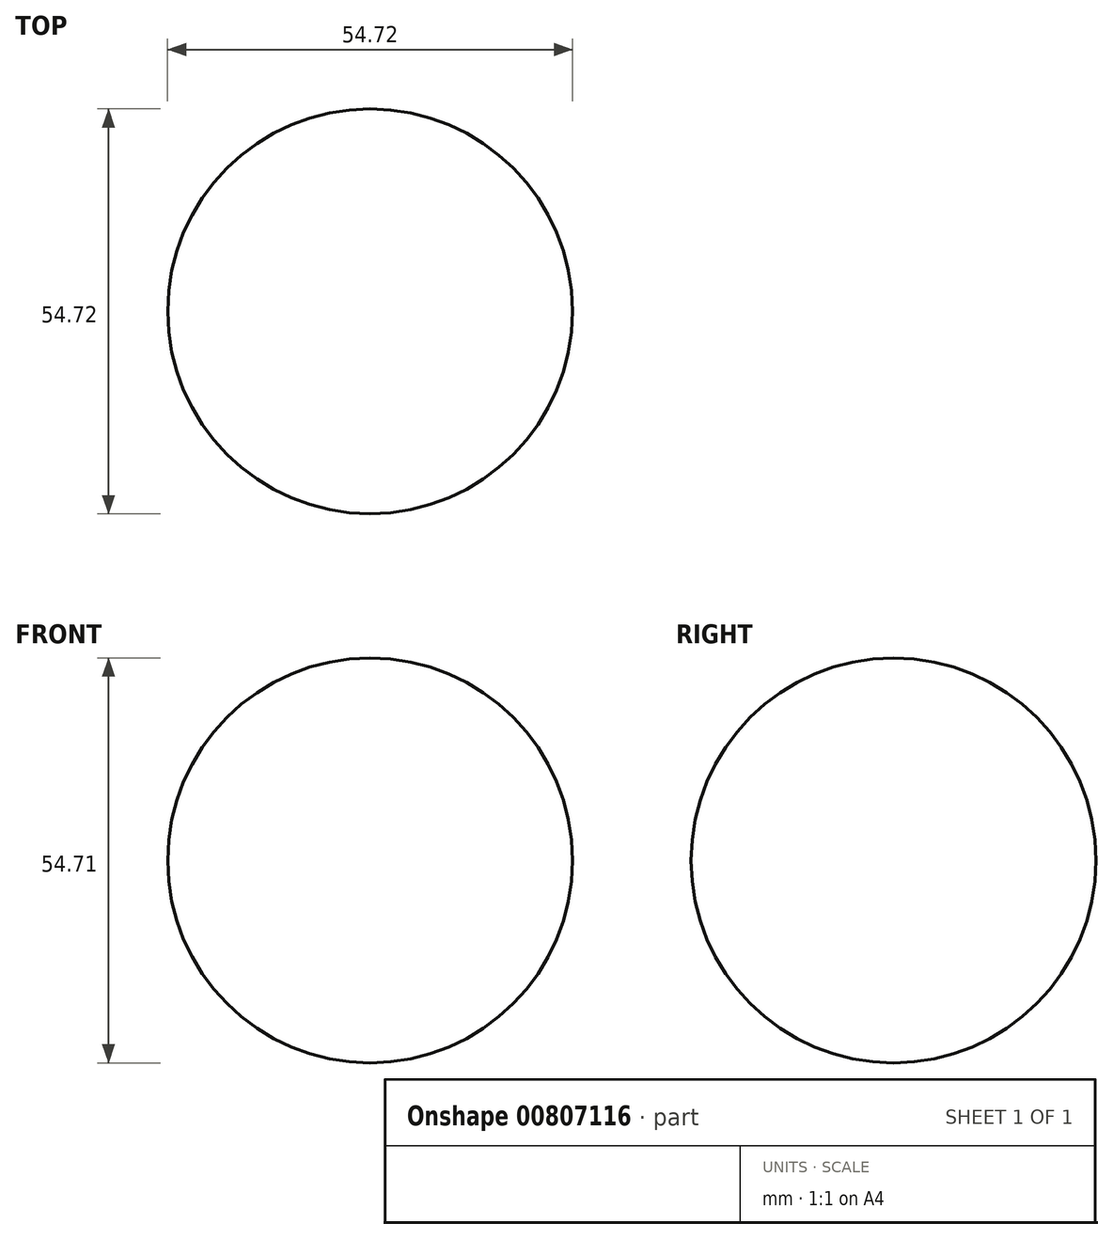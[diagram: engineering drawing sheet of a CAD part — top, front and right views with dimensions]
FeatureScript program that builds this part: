
annotation { "Feature Type Name" : "Feature", "Feature Type Description" : "" }
export const myFeature = defineFeature(function(context is Context, id is Id, definition is map)
    precondition{}
    {
        {
            var Q0;
            Q0=qCreatedBy(makeId("Front.planeOp"),FACE);
            var sketch = newSketch(context, id + "F0", { "sketchPlane" : qUnion([Q0])});
            skCircle(sketch, "E0", {"center": v(0, 9.22) * mm, "radius": 27.36 * mm});
            skLineSegment(sketch, "E1", {"start": v(-32.23, 9.22) * mm, "end": v(34.7, 9.22) * mm});
            skSolve(sketch);
        }
        {
            var Q0;
            {var subQ0=sQuery(id+"F0.wireOp",EDGE,"E1");var subQ1=sQuery(id+"F0.wireOp",EDGE,"E0");var subQ2=makeQuery(id+"F0.imprint","INTERSECT",VERTEX,{"disambiguationData":[OD(0.0)],"derivedFrom":[subQ1,subQ0]});Q0=makeQuery(id+"F0.imprint","IMPRINT",FACE,{"disambiguationData":[TD([[makeQuery(id+"F0.imprint","IMPRINT",EDGE,{"disambiguationData":[TD([[subQ2,-1.0]])],"derivedFrom":subQ1}),1.0]])]});}
            var Q1;
            Q1=sQuery(id+"F0.wireOp",EDGE,"E1");
            revolve(context, id + "F1", {"surfaceOperationType" : NewSurfaceOperationType.NEW, "entities" : qUnion([Q0]), "axis" : qUnion([Q1]), "revolveType" : RevolveType.FULL});
        }
    });
